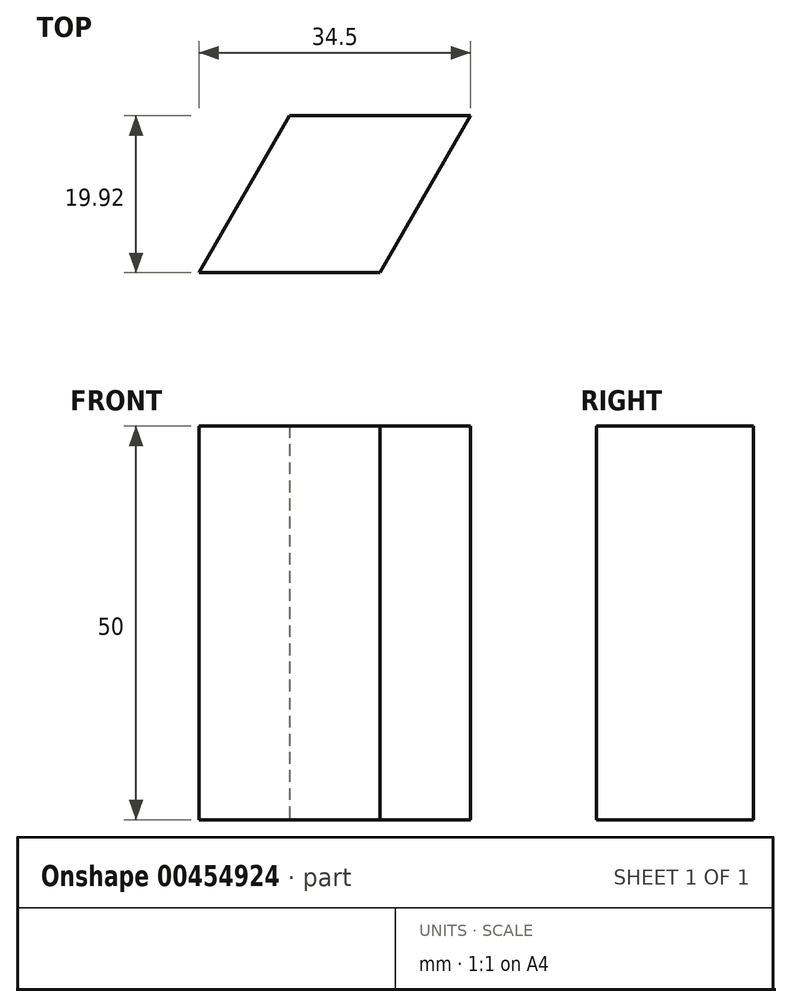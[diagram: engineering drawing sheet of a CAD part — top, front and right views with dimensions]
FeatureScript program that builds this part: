
annotation { "Feature Type Name" : "Feature", "Feature Type Description" : "" }
export const myFeature = defineFeature(function(context is Context, id is Id, definition is map)
    precondition{}
    {
        {
            var Q0;
            Q0=qCreatedBy(makeId("Top.planeOp"),FACE);
            var sketch = newSketch(context, id + "F0", { "sketchPlane" : qUnion([Q0])});
            skLineSegment(sketch, "E0", {"start": v(-11.5, -9.73) * mm, "end": v(11.5, -9.73) * mm});
            skLineSegment(sketch, "E1", {"start": v(11.5, -9.73) * mm, "end": v(23, 10.19) * mm});
            skLineSegment(sketch, "E2", {"start": v(23, 10.19) * mm, "end": v(0, 10.19) * mm});
            skLineSegment(sketch, "E3", {"start": v(0, 10.19) * mm, "end": v(-11.5, -9.73) * mm});
            skPoint(sketch, "E4", {"position": v(0, 0) * mm});
            skSolve(sketch);
        }
        {
            var Q0;
            Q0 = qSketchRegion(id + "F0", true);
            var sketch = newSketch(context, id + "F1", { "sketchPlane" : qUnion([Q0])});
            skSolve(sketch);
        }
        {
            var Q0;
            Q0=makeQuery(id+"F0.imprint","IMPRINT",FACE,{"disambiguationData":[TD([[makeQuery(id+"F0.imprint","IMPRINT",EDGE,{"derivedFrom":sQuery(id+"F0.wireOp",EDGE,"E0")}),1.0]])]});
            var Q1;
            Q1=sQuery(id+"F0.wireOp",EDGE,"E0");
            var Q2;
            Q2=sQuery(id+"F0.wireOp",EDGE,"E1");
            var Q3;
            Q3=sQuery(id+"F0.wireOp",EDGE,"E3");
            var Q4;
            Q4=sQuery(id+"F0.wireOp",EDGE,"E2");
            extrude(context, id + "F2", {"entities" : qUnion([Q0]), "surfaceEntities" : qUnion([Q1, Q2, Q3, Q4]), "depth" : 50 * mm});
        }
    });
